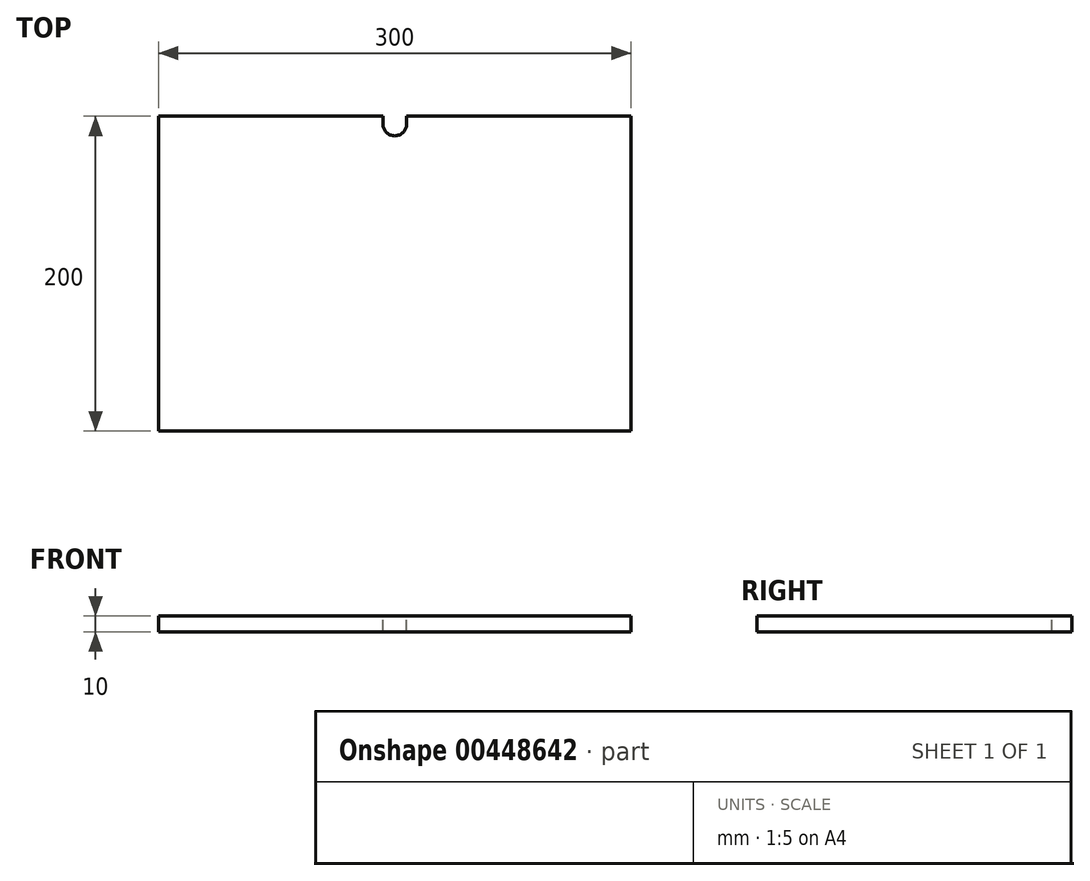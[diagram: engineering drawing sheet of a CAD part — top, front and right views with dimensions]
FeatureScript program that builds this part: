
annotation { "Feature Type Name" : "Feature", "Feature Type Description" : "" }
export const myFeature = defineFeature(function(context is Context, id is Id, definition is map)
    precondition{}
    {
        {
            var Q0;
            Q0=qCreatedBy(makeId("Top.planeOp"),FACE);
            var sketch = newSketch(context, id + "F0", { "sketchPlane" : qUnion([Q0])});
            skLineSegment(sketch, "E0.bottom", {"start": v(-150, 100) * mm, "end": v(150, 100) * mm});
            skLineSegment(sketch, "E0.top", {"start": v(-150, -100) * mm, "end": v(150, -100) * mm});
            skLineSegment(sketch, "E0.left", {"start": v(-150, 100) * mm, "end": v(-150, -100) * mm});
            skLineSegment(sketch, "E0.right", {"start": v(150, 100) * mm, "end": v(150, -100) * mm});
            skPoint(sketch, "E0.middle", {"position": v(0, 0) * mm});
            skSolve(sketch);
        }
        {
            var Q0;
            Q0=makeQuery(id+"F0.imprint","IMPRINT",FACE,{"disambiguationData":[TD([[makeQuery(id+"F0.imprint","IMPRINT",EDGE,{"derivedFrom":sQuery(id+"F0.wireOp",EDGE,"E0.bottom")}),-1.0]])]});
            extrude(context, id + "F1", {"entities" : qUnion([Q0]), "endBound" : BoundingType.SYMMETRIC, "depth" : 10 * mm});
        }
        {
            var Q0;
            Q0=makeQuery(id+"F1.opExtrude","CAP_FACE",FACE,{"disambiguationData":[OSD([sQuery(id+"F0.wireOp",EDGE,"E0.bottom"),sQuery(id+"F0.wireOp",EDGE,"E0.top"),sQuery(id+"F0.wireOp",EDGE,"E0.left"),sQuery(id+"F0.wireOp",EDGE,"E0.right")])],"isStart":false});
            var sketch = newSketch(context, id + "F2", { "sketchPlane" : qUnion([Q0])});
            skArc(sketch, "E1", {"start": v(-7.5, 95) * mm, "mid": v(0, 87.5) * mm, "end": v(7.5, 95) * mm});
            skLineSegment(sketch, "E2", {"start": v(7.5, 95) * mm, "end": v(7.5, 100) * mm});
            skLineSegment(sketch, "E3", {"start": v(7.5, 100) * mm, "end": v(-7.5, 100) * mm});
            skLineSegment(sketch, "E4", {"start": v(-7.5, 100) * mm, "end": v(-7.5, 95) * mm});
            skSolve(sketch);
        }
        {
            var Q0;
            Q0=makeQuery(id+"F2.imprint","IMPRINT",FACE,{"disambiguationData":[TD([[makeQuery(id+"F2.imprint","IMPRINT",EDGE,{"derivedFrom":sQuery(id+"F2.wireOp",EDGE,"E1")}),1.0]])]});
            extrude(context, id + "F3", {"entities" : qUnion([Q0]), "operationType" : NewBodyOperationType.REMOVE, "oppositeDirection" : true, "depth" : 10 * mm});
        }
    });
